# Revit family: Festpunkthalterung HV2_
name_source: partatom
category: Allgemeines Modell
revit_build: Autodesk Revit 2017 (Build: 20190508_0315(x64)
units: mm (PartAtom-declared; Revit-internal decimal feet)

## family parameters
Basisbauteil = Fläche
Beim Laden mit Abzugskörper schneiden = Nein
Bemaßung runder Anschluss = Durchmesser verwenden
Gemeinsam genutzt = Ja
Kann Basisbauteil für Bewehrung sein = Nein
Raumberechnungspunkt = Nein
Teiletyp = Normal

## types (18) — shared parameters
Anzahl Rohrschellen = 3
Anzugsmoment Hammersperrkopf = 120 Nm
Artikelnummer = 00200406/fvz
Breite Material Rohrschelle = 50 mm
EAN = 4250928400017
Fabrikat = MEFA
Gewicht = 4.74 kg
Kurztext1 = Festpunkthalterung HV 2
Kurztext2 = 64 - 273 mm Fx 30 kN 111 - 163 mm
Länge = 160 mm  [stored 0.524934 ft]
Mengeneinheit = St
Rohrschellentyp = Titan HD
Stärke Material Rohrschelle = 5 mm
Vorgabe-Ansicht = 1219 mm
max. Achshöhe = 163 mm
max. Rohraußendurchmesser = 273 mm  [stored 0.895669 ft]
max. zul. Last Fx = 6.74 kip
max. zul. Last Fz = 4.05 kip
max. zul. Last Fz mit 3 Schellen = 40 kN
min. Achshöhe = 111 mm
min. Rohraußendurchmesser = 64 mm  [stored 0.209974 ft]
vpe = 1

## per-type parameters (varying)
| type | S |
| HV2 Ø64 mm | 112 mm  [stored 0.367454 ft] |
| HV2 Ø76mm | 124 mm  [stored 0.406824 ft] |
| HV2 Ø89mm | 138 mm  [stored 0.452756 ft] |
| HV2 Ø108mm | 157 mm  [stored 0.515092 ft] |
| HV2 Ø110mm | 159 mm  [stored 0.521654 ft] |
| HV2 Ø114mm | 163 mm  [stored 0.534777 ft] |
| HV2 Ø133mm | 183 mm |
| HV2 Ø135mm | 185 mm  [stored 0.606955 ft] |
| HV2 Ø140mm | 190 mm |
| HV2 Ø160mm | 210 mm  [stored 0.688976 ft] |
| HV2 Ø165mm | 215 mm |
| HV2 Ø168mm | 218 mm  [stored 0.715223 ft] |
| HV2 Ø194mm | 244 mm  [stored 0.800525 ft] |
| HV2 Ø200mm | 250 mm  [stored 0.82021 ft] |
| HV2 Ø210mm | 261 mm |
| HV2 Ø219mm | 270 mm  [stored 0.885827 ft] |
| HV2 Ø267mm | 318 mm  [stored 1.04331 ft] |
| HV2 Ø273mm | 324 mm  [stored 1.06299 ft] |

note: [stored X ft] marks values corroborated as IEEE doubles in the binary element streams (Revit-internal decimal feet)

## geometry (parser evidence)
native form markers: Sweep x3
no freeform markers — native parametric forms only
